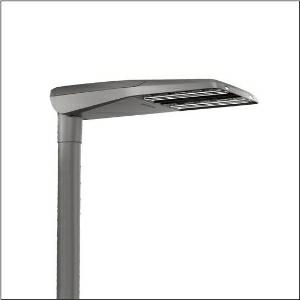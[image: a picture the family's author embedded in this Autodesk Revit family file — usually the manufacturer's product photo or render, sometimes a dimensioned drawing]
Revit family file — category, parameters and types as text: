
# Revit family: streetlight_sl_11_iq_midi___st1_2a_5xc3a11f08me_159a
name_source: partatom
category: Lighting Fixtures
units: mm (PartAtom-declared; Revit-internal decimal feet)

## family parameters
Cut with Voids When Loaded = No
Host = Face
Light Source = No
Part Type = Normal
Room Calculation Point = No
Round Connector Dimension = Use Diameter
Shared = No

## types (1)
- --- (1 x LED, 11170 lm, 124.5 W, 1800K)
    Apparent Load = 125 VA
    CIE Flux Codes = 32 70 96 100 100
    Color Rendering = 70
    Color Temperature = 1800K
    Default Elevation = 1800 mm
    Description = Streetlight SL 11 iQ midi, mast luminaire, primary light control with 3 zone facetted reflector, of plastic, silver coated, highly specular, primary optical cover: cover, of PMMA, transparent, light distribution: ST1.2a, light emission: direct distribution, primary light characteristic: asymmetric, installation type: post-top, side-entry, lamps: LED, High Power LED, rated values: 11.170lm | 124,5W | 89,7lm/W (begin service life); end service life: 11.170lm | 131,6W; at 50% lumin. flux: 5.585lm | 55,1W | 101,4lm/W, colour temperature: 1800K, colour rendering: CRI > 70, light colour: 718, light setting 1 begin service life: 100% | 11.170lm | 124,5W | 89,7lm/W | 1.800K, light setting 1 end service life: 131,6W, further light settings possible, control: Street-Remote, Auto-Match, Temp-Guard, Lumen-Switch, Night-Set, Smart-Wire, Light-Fading, Desk-Remote (wireless, voltage-free reading and setting of iQ features in the workshop via application-optimized NFC function/RFID function), optimised constant luminous flux control (CLO 2.0), with cable H07RN-F 5x 1.5mm², mains connection: 230..240V, AC, 50/60Hz, connection cable pre-assembled, cable length: 12,5m, luminaire housing, of diecast aluminium, powder-coated, Siteco® metallic grey (DB 702S), please order mast flange separately, inclination adjustable without tools: 0°, 5°, 10°, 15° (post-top) | 0°, -5°, -10°, -15° (side-entry), sealing non-destructively replaceable, multi-level sealing system, length: 780mm, width: 376mm, height: 118mm, mast flange for spigot size: 42mm (side-entry): 5XC10008XM4, 60/48mm (side-entry/post-top): 5XC10108XM2, 76/60mm (side-entry/post-top): 5XC10108XM1, equipment: Power, protection rating (complete): IP66, insulation class (complete): insulation class II (safety insulation), certification: CE, ENEC, ENEC+, VDE, impact resistance: IK10, permissible operating ambient temperature for outdoor applications: -25..+50°C, standard-compliant lighting for roads and squares, Environmental Product Declaration (EPD) tested and certified by an independent institute, packaging unit: 1 piece

Light Distribution: ST1.2a
    Height = 118 mm
    Lamp = 1 x LED
    Lamp Light Flux = 11170 lm
    Lamp Power = 124.5 W
    Lamp count = 1
    Length = 780 mm
    Luminous efficacy = 90 lm/W
    Manufacturer = Siteco
    ModVariant = No
    Model = 5XC3A11F08ME
    Number of Poles = 1
    OnlyDefault = Yes
    Power Factor = 1
    Product Name = Streetlight SL 11 iQ midi | ST1.2a
    Product group = mast luminaire | pylon top
    ProductGroupID = 6100
    Protection Class = Protection class II
    Protection Degree = IP 66
    RLX_Detail_Level = 1
    RLX_Emergency_Light_Flux = 0 lm
    RLX_Emergency_Type = 0
    RLX_Emergency_Type_DB = No
    RlxData = <blob elided: 70941 chars, md5=8cb18857>
    Socket = socket
    Standby Power = 0 W
    System Light Flux = 11170 lm
    System Power = 125 W
    Type Comments = factory setting: luminous flux: 100 % | dim-lin: 254 | 554 mA
    Type Image = l_1005960.jpg
    URL = http://relux.com
    VarID = @adj_078378
    Voltage = 0 V
    Weight = 0.00 kg
    Width = 376 mm

## geometry (parser evidence)
native form markers: Blend x4, Sweep x11
no freeform markers — native parametric forms only
